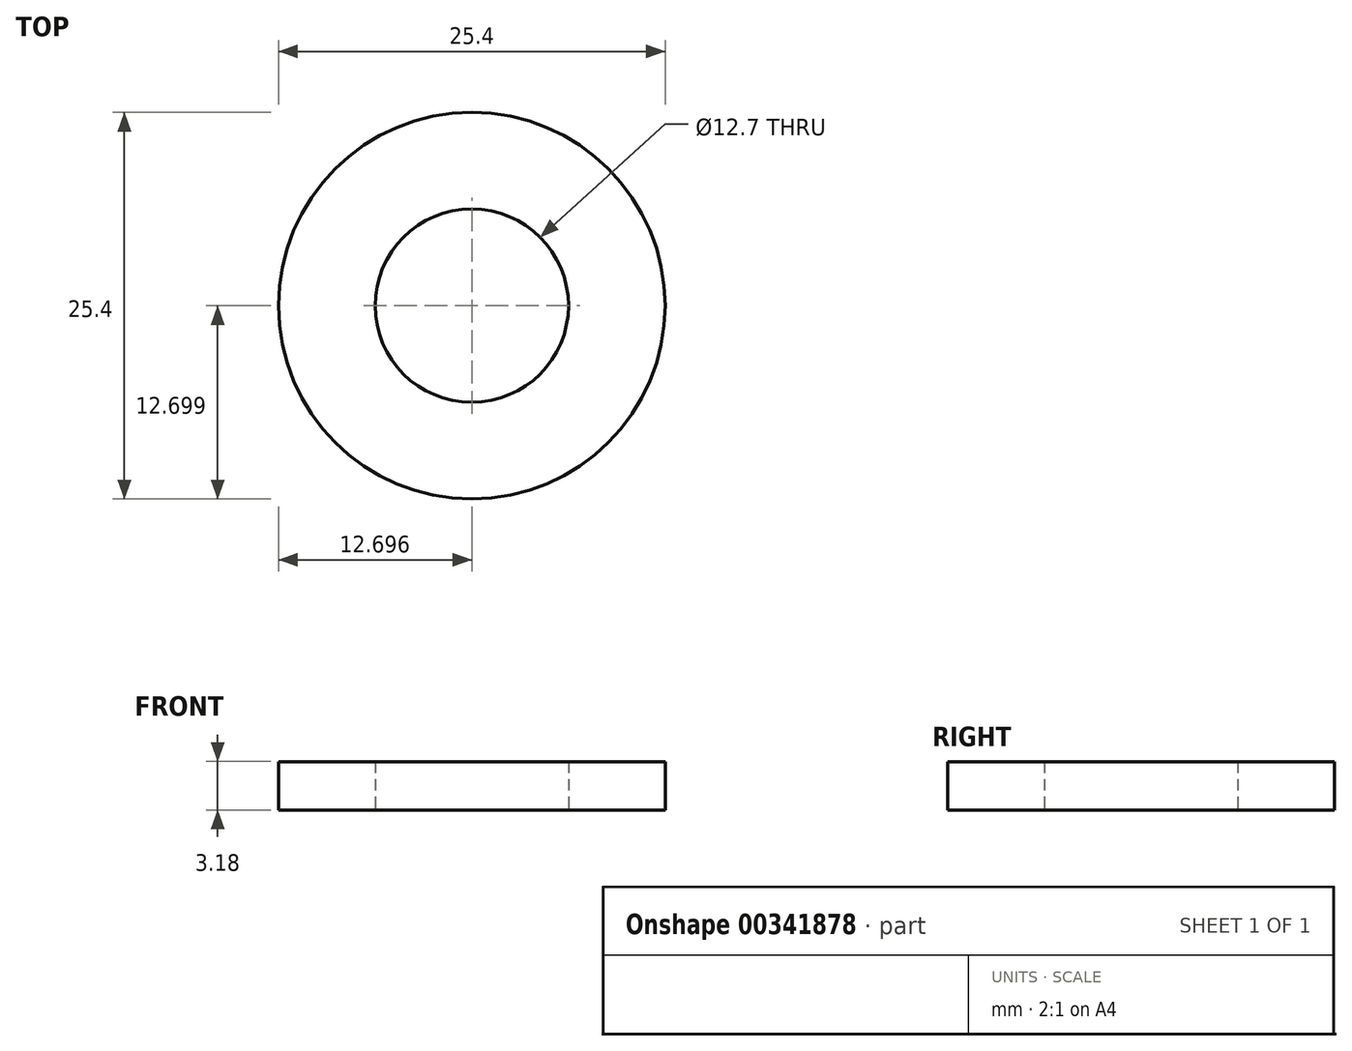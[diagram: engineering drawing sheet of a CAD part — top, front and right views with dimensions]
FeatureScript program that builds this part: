
annotation { "Feature Type Name" : "Feature", "Feature Type Description" : "" }
export const myFeature = defineFeature(function(context is Context, id is Id, definition is map)
    precondition{}
    {
        {
            var Q0;
            Q0=qCreatedBy(makeId("Top.planeOp"),FACE);
            var sketch = newSketch(context, id + "F0", { "sketchPlane" : qUnion([Q0])});
            skCircle(sketch, "E0", {"center": v(-44.73, 14.7) * mm, "radius": 12.7 * mm});
            skCircle(sketch, "E1", {"center": v(-44.73, 14.7) * mm, "radius": 6.35 * mm});
            skCircle(sketch, "E2", {"center": v(-197.64, 11.15) * mm, "radius": 38.93 * mm});
            skCircle(sketch, "E3", {"center": v(-158.85, 7.92) * mm, "radius": 38.54 * mm});
            skSolve(sketch);
        }
        {
            var Q0;
            Q0=makeQuery(id+"F0.imprint","IMPRINT",FACE,{"disambiguationData":[TD([[makeQuery(id+"F0.imprint","IMPRINT",EDGE,{"derivedFrom":sQuery(id+"F0.wireOp",EDGE,"E0")}),1.0]])]});
            extrude(context, id + "F1", {"entities" : qUnion([Q0]), "depth" : 3.17 * mm});
        }
    });
